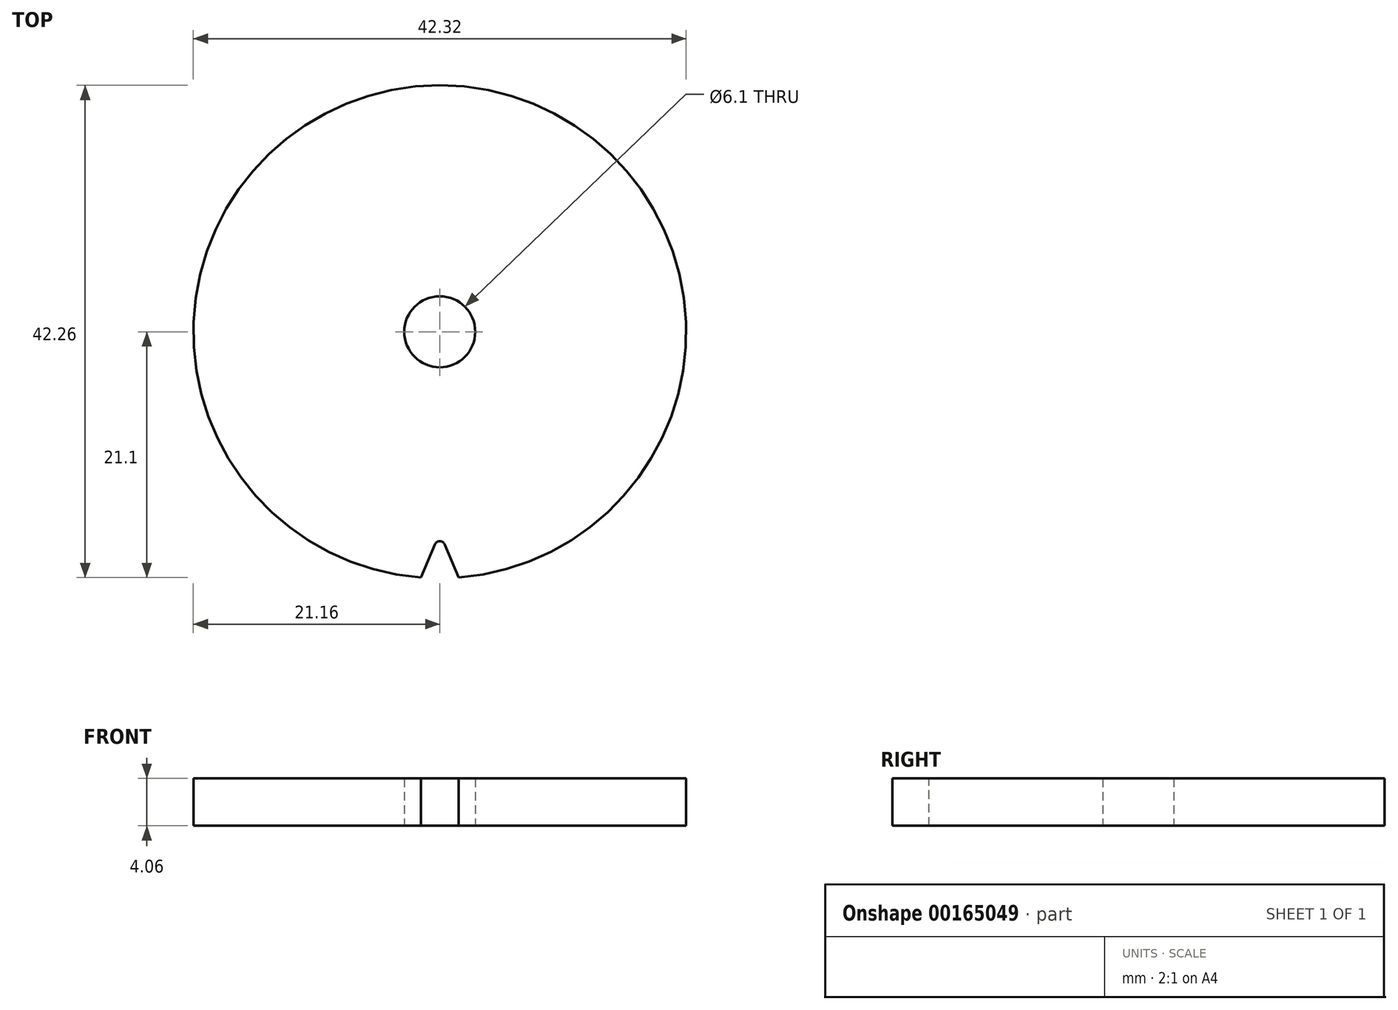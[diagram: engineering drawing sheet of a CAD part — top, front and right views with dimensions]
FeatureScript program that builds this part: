
annotation { "Feature Type Name" : "Feature", "Feature Type Description" : "" }
export const myFeature = defineFeature(function(context is Context, id is Id, definition is map)
    precondition{}
    {
        {
            var Q0;
            Q0=qCreatedBy(makeId("Top.planeOp"),FACE);
            var sketch = newSketch(context, id + "F0", { "sketchPlane" : qUnion([Q0])});
            skCircle(sketch, "E0", {"center": v(0, 0) * mm, "radius": 3.05 * mm});
            skCircle(sketch, "E1", {"center": v(0, 0) * mm, "radius": 21.16 * mm});
            skSolve(sketch);
        }
        {
            var Q0;
            Q0=qSketchRegion(id+"F0",true);
            extrude(context, id + "F1", {"entities" : qUnion([Q0]), "depth" : 4.06 * mm});
        }
        {
            var Q0;
            Q0=makeQuery(id+"F1.opExtrude","CAP_FACE",FACE,{"disambiguationData":[OSD([sQuery(id+"F0.wireOp",EDGE,"E0"),sQuery(id+"F0.wireOp",EDGE,"E1")])],"isStart":false});
            var sketch = newSketch(context, id + "F2", { "sketchPlane" : qUnion([Q0])});
            skLineSegment(sketch, "E2", {"start": v(0, 0) * mm, "end": v(0, -21.16) * mm, "construction": true});
            skArc(sketch, "E3", {"start": v(-1.62, -21.1) * mm, "mid": v(0, -21.16) * mm, "end": v(1.62, -21.1) * mm});
            skLineSegment(sketch, "E4", {"start": v(-1.62, -21.1) * mm, "end": v(-0.41, -18.25) * mm});
            skLineSegment(sketch, "E5", {"start": v(1.62, -21.1) * mm, "end": v(0.41, -18.25) * mm});
            skArc(sketch, "E6", {"start": v(0.41, -18.25) * mm, "mid": v(0, -17.97) * mm, "end": v(-0.41, -18.25) * mm});
            skLineSegment(sketch, "E7", {"start": v(-1.1, -21.13) * mm, "end": v(0, 0) * mm, "construction": true});
            skPoint(sketch, "E8", {"position": v(-1.01, -19.67) * mm});
            skSolve(sketch);
        }
        {
            var Q0;
            Q0 = qSketchRegion(id + "F2", true);
            var Q1;
            Q1=makeQuery(id+"F1.opExtrude","CAP_FACE",FACE,{"disambiguationData":[OSD([sQuery(id+"F0.wireOp",EDGE,"E0"),sQuery(id+"F0.wireOp",EDGE,"E1")])],"isStart":true});
            extrude(context, id + "F3", {"entities" : qUnion([Q0]), "operationType" : NewBodyOperationType.REMOVE, "endBound" : BoundingType.UP_TO_SURFACE, "oppositeDirection" : true, "endBoundEntityFace" : qUnion([Q1]), "depth" : 25.4 * mm});
        }
    });
